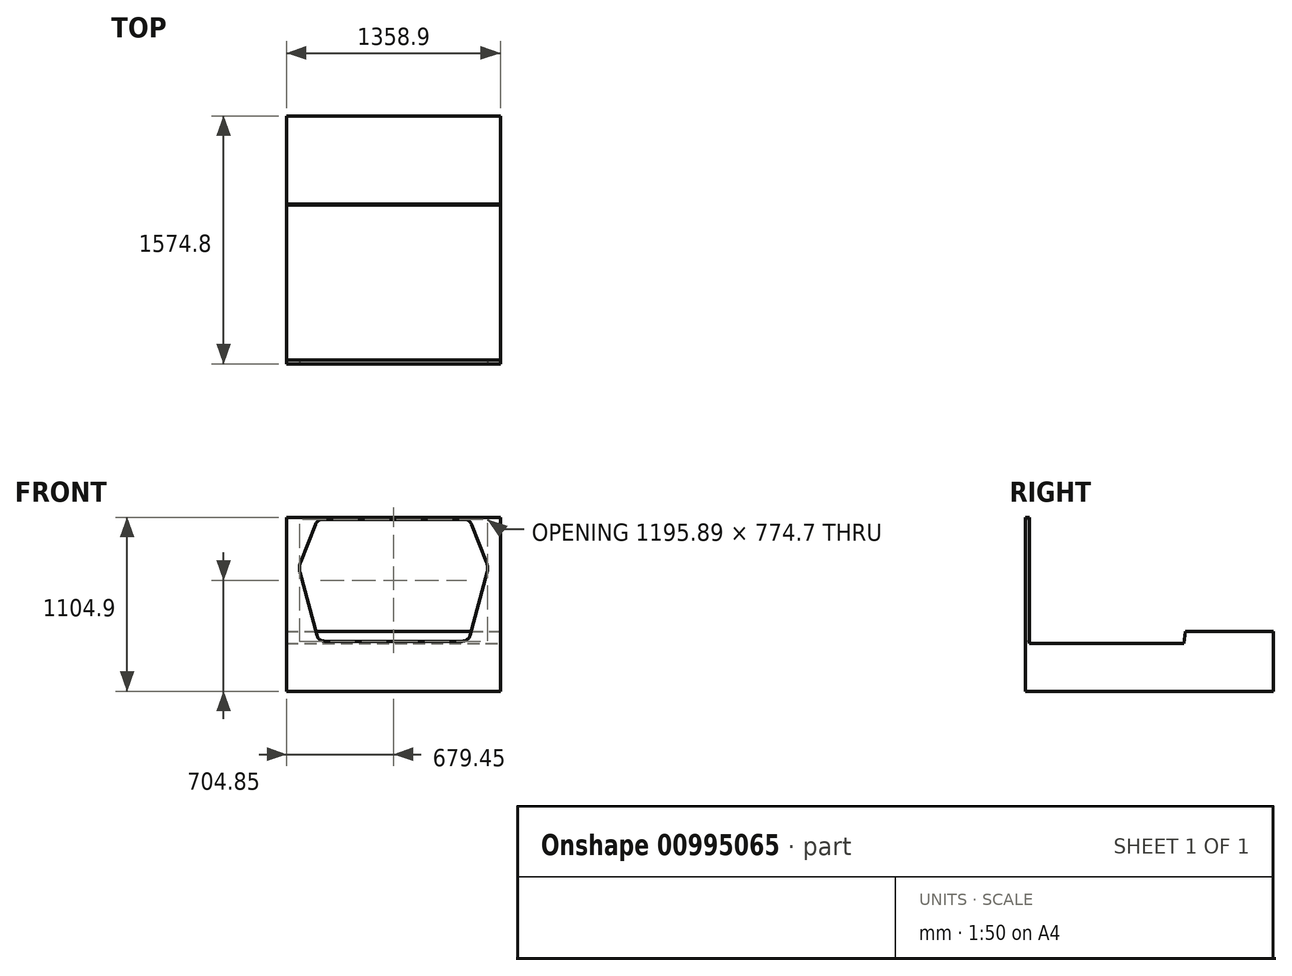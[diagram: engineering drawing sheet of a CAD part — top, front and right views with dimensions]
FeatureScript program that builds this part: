
annotation { "Feature Type Name" : "Feature", "Feature Type Description" : "" }
export const myFeature = defineFeature(function(context is Context, id is Id, definition is map)
    precondition{}
    {
        {
            var Q0;
            Q0=qCreatedBy(makeId("Top.planeOp"),FACE);
            var sketch = newSketch(context, id + "F0", { "sketchPlane" : qUnion([Q0])});
            skLineSegment(sketch, "E0.bottom", {"start": v(0, 0) * mm, "end": v(1358.9, 0) * mm});
            skLineSegment(sketch, "E0.top", {"start": v(0, 939.8) * mm, "end": v(1358.9, 939.8) * mm});
            skLineSegment(sketch, "E0.left", {"start": v(0, 0) * mm, "end": v(0, 939.8) * mm});
            skLineSegment(sketch, "E0.right", {"start": v(1358.9, 0) * mm, "end": v(1358.9, 939.8) * mm});
            skLineSegment(sketch, "E1.top", {"start": v(0, 1574.8) * mm, "end": v(1358.9, 1574.8) * mm});
            skLineSegment(sketch, "E1.left", {"start": v(0, 939.8) * mm, "end": v(0, 1574.8) * mm});
            skLineSegment(sketch, "E1.right", {"start": v(1358.9, 939.8) * mm, "end": v(1358.9, 1574.8) * mm});
            skSolve(sketch);
        }
        {
            var Q0;
            Q0=makeQuery(id+"F0.imprint","IMPRINT",FACE,{"disambiguationData":[TD([[makeQuery(id+"F0.imprint","IMPRINT",EDGE,{"derivedFrom":sQuery(id+"F0.wireOp",EDGE,"E0.top")}),1.0]])]});
            var Q1;
            Q1=makeQuery(id+"F0.imprint","IMPRINT",FACE,{"disambiguationData":[TD([[makeQuery(id+"F0.imprint","IMPRINT",EDGE,{"derivedFrom":sQuery(id+"F0.wireOp",EDGE,"E0.bottom")}),1.0]])]});
            extrude(context, id + "F1", {"entities" : qUnion([Q0, Q1]), "oppositeDirection" : true, "depth" : 304.8 * mm, "offsetDistance" : 25.4 * mm});
        }
        {
            var Q0;
            Q0=makeQuery(id+"F0.imprint","IMPRINT",FACE,{"disambiguationData":[TD([[makeQuery(id+"F0.imprint","IMPRINT",EDGE,{"derivedFrom":sQuery(id+"F0.wireOp",EDGE,"E0.top")}),1.0]])]});
            extrude(context, id + "F2", {"entities" : qUnion([Q0]), "operationType" : NewBodyOperationType.ADD, "depth" : 76.2 * mm, "offsetDistance" : 25.4 * mm});
        }
        {
            var Q0;
            Q0=makeQuery(id+"F2.opExtrude","CAP_EDGE",EDGE,{"disambiguationData":[OSD([sQuery(id+"F0.wireOp",EDGE,"E0.top")])],"isStart":false});
            chamfer(context, id + "F3", {"entities" : qUnion([Q0]), "chamferType" : ChamferType.TWO_OFFSETS, "width1" : 635 * mm, "oppositeDirection" : false, "width2" : 76.2 * mm, "tangentPropagation" : true});
        }
        {
            var Q0;
            Q0=makeQuery(id+"F1.opExtrude","SWEPT_FACE",FACE,{"disambiguationData":[OSD([sQuery(id+"F0.wireOp",EDGE,"E0.bottom")])]});
            var sketch = newSketch(context, id + "F4", { "sketchPlane" : qUnion([Q0])});
            skLineSegment(sketch, "E2.bottom", {"start": v(0, 0) * mm, "end": v(1358.9, 0) * mm});
            skLineSegment(sketch, "E2.top", {"start": v(0, 800.1) * mm, "end": v(1358.9, 800.1) * mm});
            skLineSegment(sketch, "E2.left", {"start": v(0, 0) * mm, "end": v(0, 800.1) * mm});
            skLineSegment(sketch, "E2.right", {"start": v(1358.9, 0) * mm, "end": v(1358.9, 800.1) * mm});
            skLineSegment(sketch, "E3", {"start": v(242.1, 12.7) * mm, "end": v(1116.8, 12.7) * mm});
            skLineSegment(sketch, "E4", {"start": v(231.38, 787.4) * mm, "end": v(1127.52, 787.4) * mm});
            skLineSegment(sketch, "E5", {"start": v(76.2, 482.6) * mm, "end": v(1282.7, 482.6) * mm});
            skLineSegment(sketch, "E6", {"start": v(88.61, 513.95) * mm, "end": v(184.14, 755.3) * mm});
            skLineSegment(sketch, "E7", {"start": v(85, 450.05) * mm, "end": v(193.05, 50.25) * mm});
            skLineSegment(sketch, "E8", {"start": v(1165.85, 50.25) * mm, "end": v(1273.9, 450.05) * mm});
            skLineSegment(sketch, "E9", {"start": v(1270.29, 513.95) * mm, "end": v(1174.76, 755.3) * mm});
            skPoint(sketch, "E10.visualSharp", {"position": v(196.85, 787.4) * mm});
            skArc(sketch, "E10.filletArc", {"start": v(231.38, 787.4) * mm, "mid": v(202.82, 778.61) * mm, "end": v(184.14, 755.3) * mm});
            skPoint(sketch, "E11.visualSharp", {"position": v(1162.05, 787.4) * mm});
            skArc(sketch, "E11.filletArc", {"start": v(1174.76, 755.3) * mm, "mid": v(1156.08, 778.61) * mm, "end": v(1127.52, 787.4) * mm});
            skPoint(sketch, "E12.visualSharp", {"position": v(76.2, 482.6) * mm});
            skArc(sketch, "E12.filletArc", {"start": v(88.61, 513.95) * mm, "mid": v(81.64, 482.3) * mm, "end": v(85, 450.05) * mm});
            skPoint(sketch, "E13.visualSharp", {"position": v(1282.7, 482.6) * mm});
            skArc(sketch, "E13.filletArc", {"start": v(1273.9, 450.05) * mm, "mid": v(1277.26, 482.3) * mm, "end": v(1270.29, 513.95) * mm});
            skPoint(sketch, "E14.visualSharp", {"position": v(203.2, 12.7) * mm});
            skArc(sketch, "E14.filletArc", {"start": v(193.05, 50.25) * mm, "mid": v(211.21, 23.16) * mm, "end": v(242.1, 12.7) * mm});
            skPoint(sketch, "E15.visualSharp", {"position": v(1155.7, 12.7) * mm});
            skArc(sketch, "E15.filletArc", {"start": v(1116.8, 12.7) * mm, "mid": v(1147.69, 23.16) * mm, "end": v(1165.85, 50.25) * mm});
            skSolve(sketch);
        }
        {
            var Q0;
            Q0=makeQuery(id+"F4.imprint","IMPRINT",FACE,{"disambiguationData":[TD([[makeQuery(id+"F4.imprint","IMPRINT",EDGE,{"derivedFrom":sQuery(id+"F4.wireOp",EDGE,"E2.bottom")}),1.0]])]});
            extrude(context, id + "F5", {"entities" : qUnion([Q0]), "operationType" : NewBodyOperationType.ADD, "oppositeDirection" : true, "depth" : 25.4 * mm, "offsetDistance" : 25.4 * mm});
        }
    });
